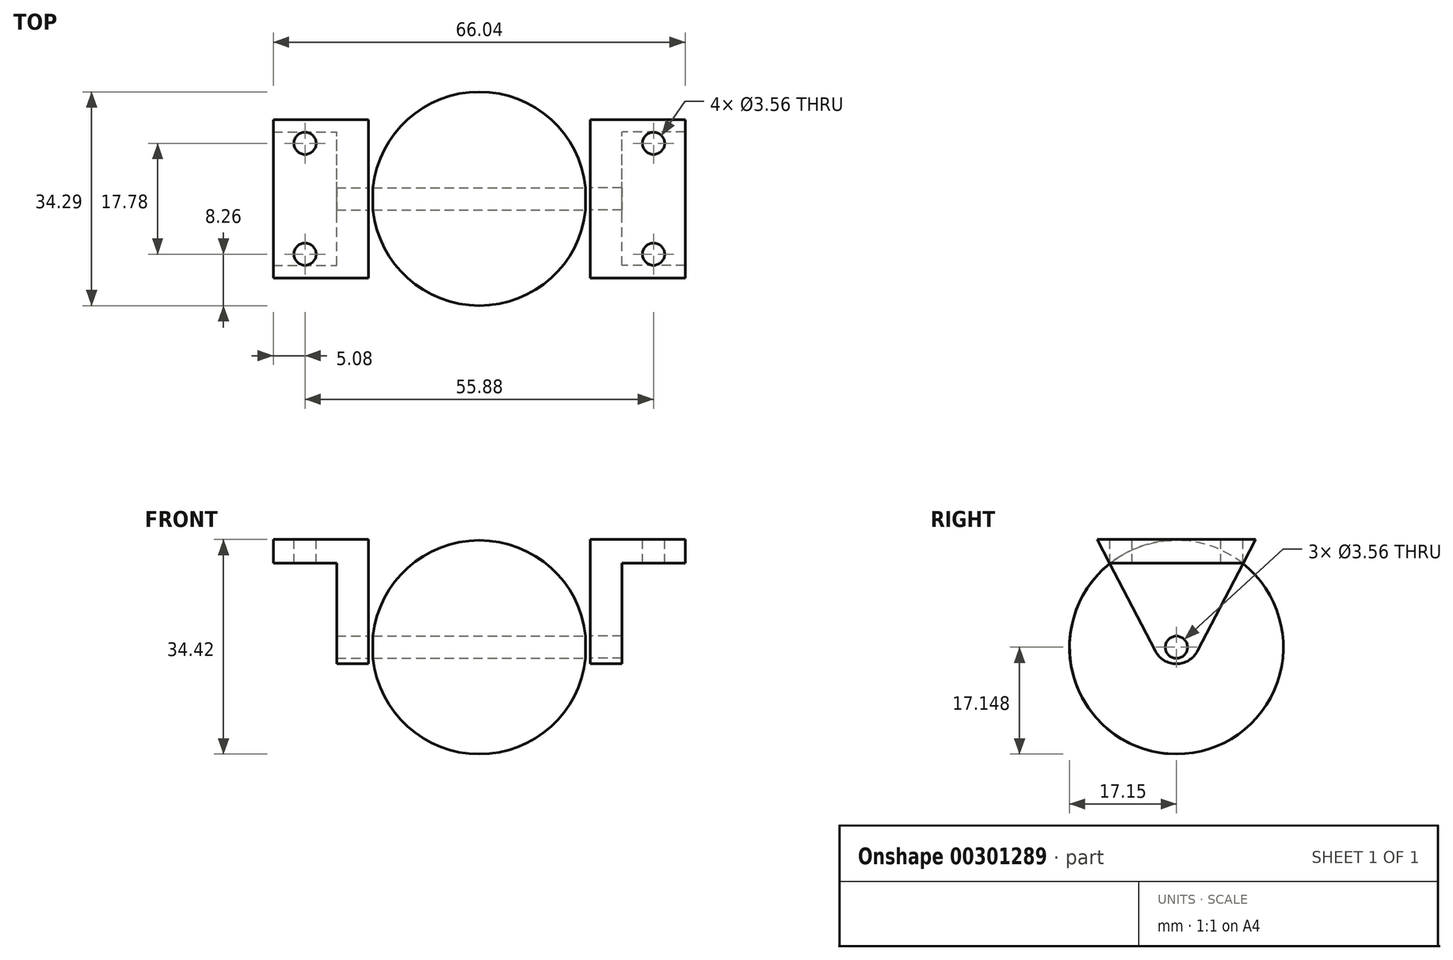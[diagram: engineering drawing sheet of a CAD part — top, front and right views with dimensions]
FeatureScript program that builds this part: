
annotation { "Feature Type Name" : "Feature", "Feature Type Description" : "" }
export const myFeature = defineFeature(function(context is Context, id is Id, definition is map)
    precondition{}
    {
        {
            var Q0;
            Q0=qCreatedBy(makeId("Right.planeOp"),FACE);
            var sketch = newSketch(context, id + "F0", { "sketchPlane" : qUnion([Q0])});
            skLineSegment(sketch, "E0", {"start": v(0, 0) * mm, "end": v(12.7, -24.38) * mm});
            skLineSegment(sketch, "E1", {"start": v(12.7, -24.38) * mm, "end": v(25.4, 0) * mm});
            skLineSegment(sketch, "E2", {"start": v(25.4, 0) * mm, "end": v(0, 0) * mm});
            skCircle(sketch, "E3", {"center": v(12.7, -17.27) * mm, "radius": 1.78 * mm});
            skSolve(sketch);
        }
        {
            var Q0;
            Q0=qCreatedBy(makeId("Right.planeOp"),FACE);
            var sketch = newSketch(context, id + "F1", { "sketchPlane" : qUnion([Q0])});
            skPoint(sketch, "E4", {"position": v(12.7, -17.27) * mm});
            skArc(sketch, "E5", {"start": v(12.7, -0.13) * mm, "mid": v(-4.44, -17.27) * mm, "end": v(12.7, -34.42) * mm});
            skLineSegment(sketch, "E6", {"start": v(12.7, -0.13) * mm, "end": v(12.7, -34.42) * mm});
            skSolve(sketch);
        }
        {
            var Q0;
            Q0=makeQuery(id+"F1.imprint","IMPRINT",FACE,{"disambiguationData":[TD([[makeQuery(id+"F1.imprint","IMPRINT",EDGE,{"derivedFrom":sQuery(id+"F1.wireOp",EDGE,"E5")}),1.0]])]});
            var Q1;
            Q1=sQuery(id+"F1.wireOp",EDGE,"E6");
            revolve(context, id + "F2", {"entities" : qUnion([Q0]), "axis" : qUnion([Q1]), "revolveType" : RevolveType.FULL});
        }
        {
            var Q0;
            Q0=qCreatedBy(makeId("Right.planeOp"),FACE);
            var sketch = newSketch(context, id + "F3", { "sketchPlane" : qUnion([Q0])});
            skCircle(sketch, "E7", {"center": v(12.7, -17.27) * mm, "radius": 1.78 * mm});
            skSolve(sketch);
        }
        {
            var Q0;
            Q0 = qSketchRegion(id + "F3", true);
            extrude(context, id + "F4", {"entities" : qUnion([Q0]), "operationType" : NewBodyOperationType.REMOVE, "oppositeDirection" : true, "depth" : 25.4 * mm, "hasSecondDirection" : true, "secondDirectionOppositeDirection" : false, "secondDirectionDepth" : 25.4 * mm});
        }
        {
            var Q0;
            Q0 = qSketchRegion(id + "F0", true);
            extrude(context, id + "F5", {"entities" : qUnion([Q0]), "depth" : 5.08 * mm});
        }
        {
            var Q0;
            Q0=makeQuery(id+"F5.opExtrude","SWEPT_BODY",BODY,{"disambiguationData":[OSD([sQuery(id+"F0.wireOp",EDGE,"E0"),sQuery(id+"F0.wireOp",EDGE,"E1"),sQuery(id+"F0.wireOp",EDGE,"E2"),sQuery(id+"F0.wireOp",EDGE,"E3")])]});
            transform(context, id + "F6", {"entities" : qUnion([Q0]), "transformType" : TransformType.TRANSLATION_3D, "dx" : 17.78 * mm, "dy" : 0 * mm, "dz" : 0 * mm, "makeCopy" : false});
        }
        {
            var Q0;
            Q0=makeQuery(id+"F5.opExtrude","CAP_FACE",FACE,{"disambiguationData":[OSD([sQuery(id+"F0.wireOp",EDGE,"E0"),sQuery(id+"F0.wireOp",EDGE,"E1"),sQuery(id+"F0.wireOp",EDGE,"E2"),sQuery(id+"F0.wireOp",EDGE,"E3")])],"isStart":false});
            var sketch = newSketch(context, id + "F7", { "sketchPlane" : qUnion([Q0])});
            skLineSegment(sketch, "E8", {"start": v(0, 0) * mm, "end": v(1.98, -3.8) * mm});
            skLineSegment(sketch, "E9", {"start": v(1.98, -3.81) * mm, "end": v(23.42, -3.81) * mm});
            skLineSegment(sketch, "E10", {"start": v(23.42, -3.8) * mm, "end": v(25.4, 0) * mm});
            skLineSegment(sketch, "E11", {"start": v(25.4, 0) * mm, "end": v(0, 0) * mm});
            skSolve(sketch);
        }
        {
            var Q0;
            Q0 = qSketchRegion(id + "F7", true);
            extrude(context, id + "F8", {"entities" : qUnion([Q0]), "operationType" : NewBodyOperationType.ADD, "depth" : 10.16 * mm});
        }
        {
            var Q0;
            Q0=makeQuery(id+"F8.boolean.opBoolean","MERGE",FACE,{"derivedFrom":[makeQuery(id+"F5.opExtrude","SWEPT_FACE",FACE,{"disambiguationData":[OSD([sQuery(id+"F0.wireOp",EDGE,"E2")])]}),makeQuery(id+"F8.opExtrude","SWEPT_FACE",FACE,{"disambiguationData":[OSD([sQuery(id+"F7.wireOp",EDGE,"E11")])]})]});
            var sketch = newSketch(context, id + "F9", { "sketchPlane" : qUnion([Q0])});
            skLineSegment(sketch, "E12", {"start": v(17.78, 12.7) * mm, "end": v(33.02, 12.7) * mm, "construction": true});
            skCircle(sketch, "E13", {"center": v(27.94, 21.6) * mm, "radius": 1.78 * mm});
            skCircle(sketch, "E14.MirrorC", {"center": v(27.94, 3.81) * mm, "radius": 1.78 * mm});
            skSolve(sketch);
        }
        {
            var Q0;
            Q0 = qSketchRegion(id + "F9", true);
            extrude(context, id + "F10", {"entities" : qUnion([Q0]), "operationType" : NewBodyOperationType.REMOVE, "oppositeDirection" : true, "depth" : 25.4 * mm});
        }
        {
            var Q0;
            Q0=makeQuery(id+"F5.opExtrude","SWEPT_EDGE",EDGE,{"disambiguationData":[OSD([sQuery(id+"F0.wireOp",EDGE,"E0"),sQuery(id+"F0.wireOp",EDGE,"E1")])]});
            fillet(context, id + "F11", {"entities" : qUnion([Q0]), "radius" : 3.8 * mm, "tangentPropagation" : true, "allowEdgeOverflow" : false});
        }
        {
            var Q0;
            Q0=makeQuery(id+"F5.opExtrude","SWEPT_BODY",BODY,{"disambiguationData":[OSD([sQuery(id+"F0.wireOp",EDGE,"E0"),sQuery(id+"F0.wireOp",EDGE,"E1"),sQuery(id+"F0.wireOp",EDGE,"E2"),sQuery(id+"F0.wireOp",EDGE,"E3")])]});
            var Q1;
            Q1=qCreatedBy(makeId("Right.planeOp"),FACE);
            mirror(context, id + "F12", {"entities" : qUnion([Q0]), "mirrorPlane" : qUnion([Q1])});
        }
    });
